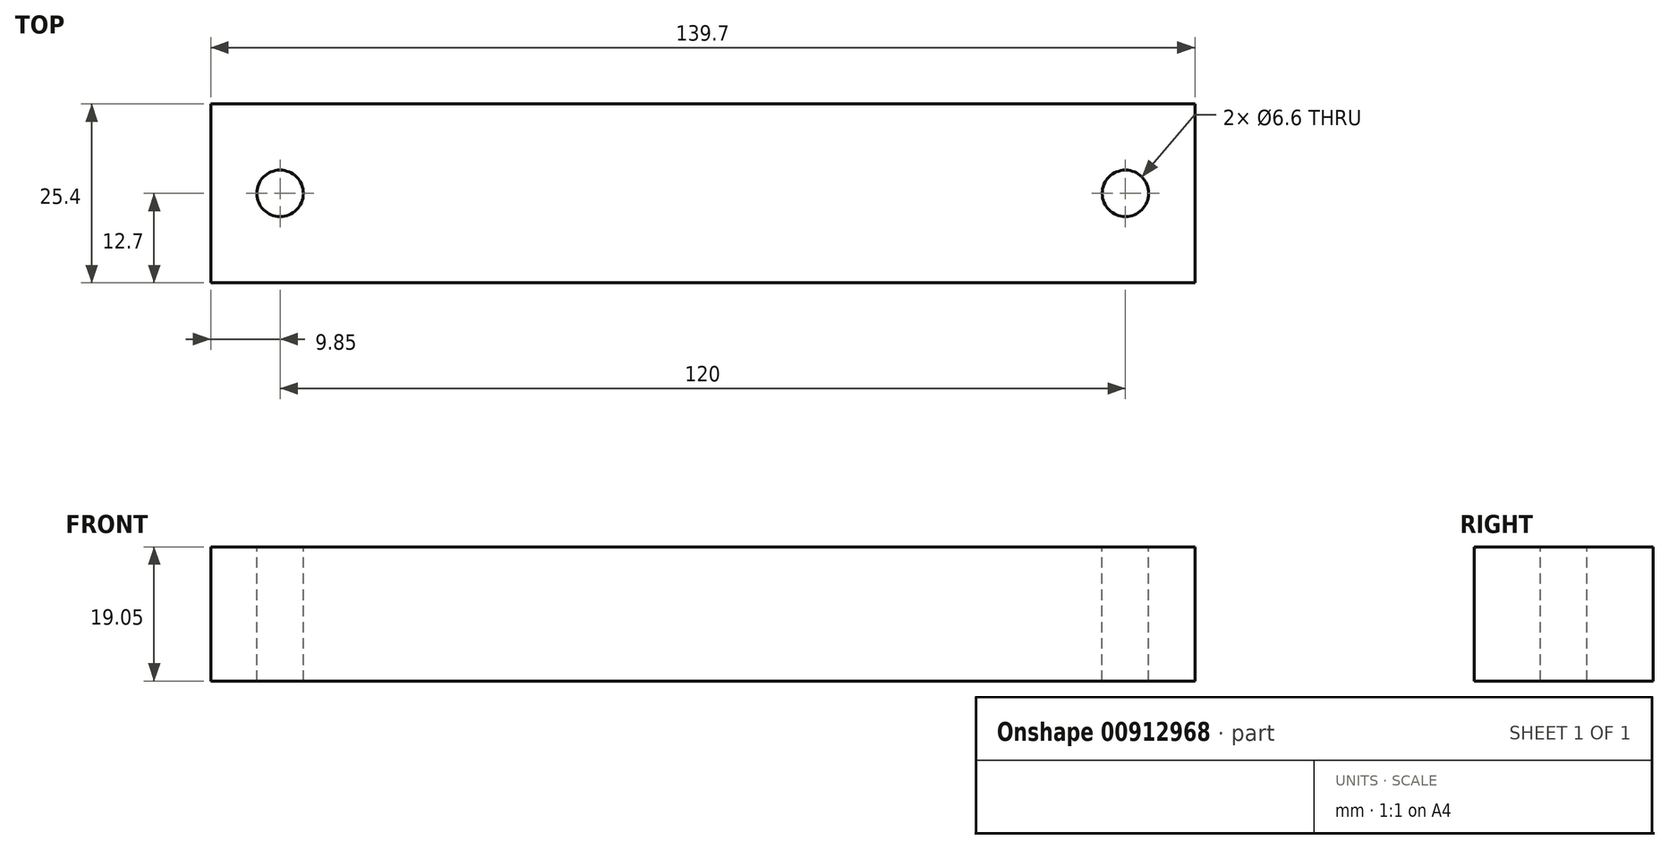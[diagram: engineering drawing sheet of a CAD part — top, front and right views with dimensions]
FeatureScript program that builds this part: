
annotation { "Feature Type Name" : "Feature", "Feature Type Description" : "" }
export const myFeature = defineFeature(function(context is Context, id is Id, definition is map)
    precondition{}
    {
        {
            var Q0;
            Q0=qCreatedBy(makeId("Top.planeOp"),FACE);
            var sketch = newSketch(context, id + "F0", { "sketchPlane" : qUnion([Q0])});
            skLineSegment(sketch, "E0.bottom", {"start": v(69.85, 12.7) * mm, "end": v(-69.85, 12.7) * mm});
            skLineSegment(sketch, "E0.top", {"start": v(69.85, -12.7) * mm, "end": v(-69.85, -12.7) * mm});
            skLineSegment(sketch, "E0.left", {"start": v(69.85, 12.7) * mm, "end": v(69.85, -12.7) * mm});
            skLineSegment(sketch, "E0.right", {"start": v(-69.85, 12.7) * mm, "end": v(-69.85, -12.7) * mm});
            skPoint(sketch, "E0.middle", {"position": v(0, 0) * mm});
            skSolve(sketch);
        }
        {
            var Q0;
            Q0 = qSketchRegion(id + "F0", true);
            extrude(context, id + "F1", {"entities" : qUnion([Q0]), "depth" : 19.05 * mm, "offsetDistance" : 25.4 * mm});
        }
        {
            var Q0;
            Q0=makeQuery(id+"F1.opExtrude","CAP_FACE",FACE,{"disambiguationData":[OSD([sQuery(id+"F0.wireOp",EDGE,"E0.bottom"),sQuery(id+"F0.wireOp",EDGE,"E0.top"),sQuery(id+"F0.wireOp",EDGE,"E0.left"),sQuery(id+"F0.wireOp",EDGE,"E0.right")])],"isStart":false});
            var sketch = newSketch(context, id + "F2", { "sketchPlane" : qUnion([Q0])});
            skLineSegment(sketch, "E1", {"start": v(-60, 0) * mm, "end": v(0, 0) * mm, "construction": true});
            skPoint(sketch, "E1.startSnap0", {"position": v(-69.85, 0) * mm});
            skLineSegment(sketch, "E2", {"start": v(0, 0) * mm, "end": v(60, 0) * mm, "construction": true});
            skCircle(sketch, "E3", {"center": v(-60, 0) * mm, "radius": 3.3 * mm});
            skCircle(sketch, "E4", {"center": v(60, 0) * mm, "radius": 3.3 * mm});
            skSolve(sketch);
        }
        {
            var Q0;
            Q0 = qSketchRegion(id + "F2", true);
            extrude(context, id + "F3", {"entities" : qUnion([Q0]), "operationType" : NewBodyOperationType.REMOVE, "endBound" : BoundingType.THROUGH_ALL, "oppositeDirection" : true, "depth" : 25.4 * mm, "offsetDistance" : 25.4 * mm});
        }
    });
